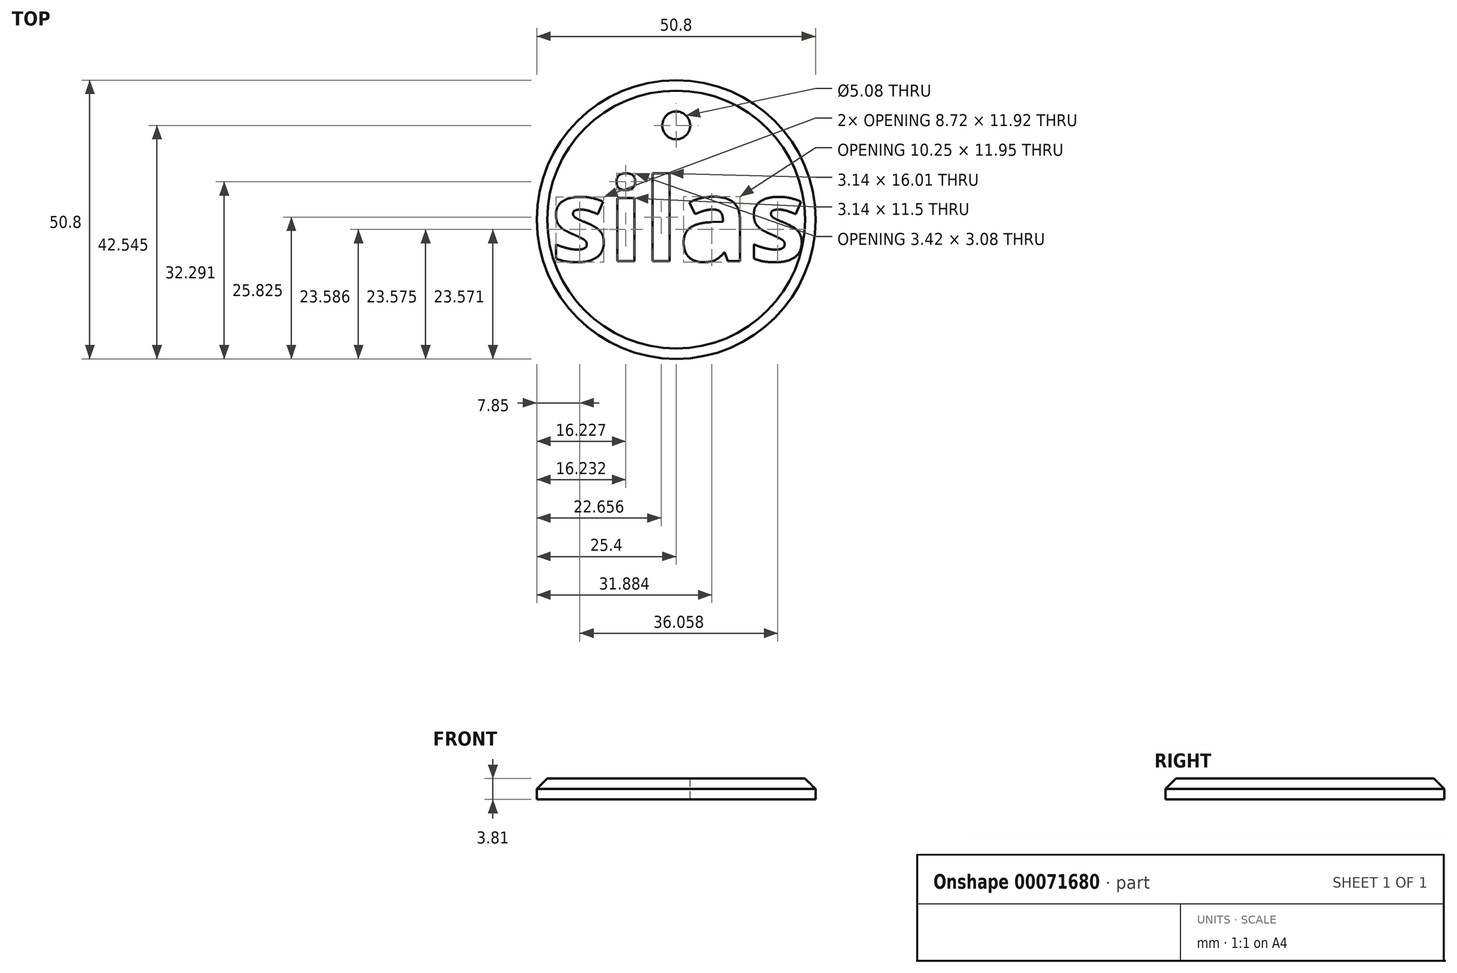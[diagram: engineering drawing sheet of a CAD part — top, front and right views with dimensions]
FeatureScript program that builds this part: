
annotation { "Feature Type Name" : "Feature", "Feature Type Description" : "" }
export const myFeature = defineFeature(function(context is Context, id is Id, definition is map)
    precondition{}
    {
        {
            var Q0;
            Q0=qCreatedBy(makeId("Top.planeOp"),FACE);
            var sketch = newSketch(context, id + "F0", { "sketchPlane" : qUnion([Q0])});
            skCircle(sketch, "E0", {"center": v(0, 0) * mm, "radius": 25.4 * mm});
            skText(sketch, "E1", { "text": "silas", "fontName": "OpenSans-Bold.ttf"});
            const initialGuessF0  = {"E1": [-0.02286, -0.00758, 1, 0, 0.01517]};
            skSetInitialGuess(sketch, initialGuessF0);
            skSolve(sketch);
        }
        {
            var Q0;
            Q0=makeQuery(id+"F0.imprint","IMPRINT",FACE,{"disambiguationData":[TD([[makeQuery(id+"F0.imprint","IMPRINT",EDGE,{"derivedFrom":sQuery(id+"F0.wireOp",EDGE,"E0")}),1.0]])]});
            extrude(context, id + "F1", {"entities" : qUnion([Q0]), "depth" : 3.8 * mm});
        }
        {
            var Q0;
            Q0=makeQuery(id+"F1.opExtrude","CAP_EDGE",EDGE,{"disambiguationData":[OSD([sQuery(id+"F0.wireOp",EDGE,"E0")])],"isStart":false});
            chamfer(context, id + "F2", {"entities" : qUnion([Q0]), "width" : 1.9 * mm, "tangentPropagation" : true});
        }
        {
            var Q0;
            Q0=makeQuery(id+"F1.opExtrude","CAP_FACE",FACE,{"disambiguationData":[OSD([sQuery(id+"F0.wireOp",EDGE,"E0"),sQuery(id+"F0.wireOp",EDGE,"E1.sketch_text.stroke-0"),sQuery(id+"F0.wireOp",EDGE,"E1.sketch_text.stroke-1"),sQuery(id+"F0.wireOp",EDGE,"E1.sketch_text.stroke-2"),sQuery(id+"F0.wireOp",EDGE,"E1.sketch_text.stroke-3"),sQuery(id+"F0.wireOp",EDGE,"E1.sketch_text.stroke-4"),sQuery(id+"F0.wireOp",EDGE,"E1.sketch_text.stroke-5"),sQuery(id+"F0.wireOp",EDGE,"E1.sketch_text.stroke-6"),sQuery(id+"F0.wireOp",EDGE,"E1.sketch_text.stroke-7"),sQuery(id+"F0.wireOp",EDGE,"E1.sketch_text.stroke-8"),sQuery(id+"F0.wireOp",EDGE,"E1.sketch_text.stroke-9"),sQuery(id+"F0.wireOp",EDGE,"E1.sketch_text.stroke-10"),sQuery(id+"F0.wireOp",EDGE,"E1.sketch_text.stroke-11"),sQuery(id+"F0.wireOp",EDGE,"E1.sketch_text.stroke-12"),sQuery(id+"F0.wireOp",EDGE,"E1.sketch_text.stroke-13"),sQuery(id+"F0.wireOp",EDGE,"E1.sketch_text.stroke-14"),sQuery(id+"F0.wireOp",EDGE,"E1.sketch_text.stroke-15"),sQuery(id+"F0.wireOp",EDGE,"E1.sketch_text.stroke-16"),sQuery(id+"F0.wireOp",EDGE,"E1.sketch_text.stroke-17"),sQuery(id+"F0.wireOp",EDGE,"E1.sketch_text.stroke-18"),sQuery(id+"F0.wireOp",EDGE,"E1.sketch_text.stroke-19"),sQuery(id+"F0.wireOp",EDGE,"E1.sketch_text.stroke-20"),sQuery(id+"F0.wireOp",EDGE,"E1.sketch_text.stroke-21"),sQuery(id+"F0.wireOp",EDGE,"E1.sketch_text.stroke-22"),sQuery(id+"F0.wireOp",EDGE,"E1.sketch_text.stroke-23"),sQuery(id+"F0.wireOp",EDGE,"E1.sketch_text.stroke-24"),sQuery(id+"F0.wireOp",EDGE,"E1.sketch_text.stroke-25"),sQuery(id+"F0.wireOp",EDGE,"E1.sketch_text.stroke-26"),sQuery(id+"F0.wireOp",EDGE,"E1.sketch_text.stroke-27"),sQuery(id+"F0.wireOp",EDGE,"E1.sketch_text.stroke-28"),sQuery(id+"F0.wireOp",EDGE,"E1.sketch_text.stroke-29"),sQuery(id+"F0.wireOp",EDGE,"E1.sketch_text.stroke-30"),sQuery(id+"F0.wireOp",EDGE,"E1.sketch_text.stroke-31"),sQuery(id+"F0.wireOp",EDGE,"E1.sketch_text.stroke-32"),sQuery(id+"F0.wireOp",EDGE,"E1.sketch_text.stroke-33"),sQuery(id+"F0.wireOp",EDGE,"E1.sketch_text.stroke-34"),sQuery(id+"F0.wireOp",EDGE,"E1.sketch_text.stroke-35"),sQuery(id+"F0.wireOp",EDGE,"E1.sketch_text.stroke-36"),sQuery(id+"F0.wireOp",EDGE,"E1.sketch_text.stroke-37"),sQuery(id+"F0.wireOp",EDGE,"E1.sketch_text.stroke-38"),sQuery(id+"F0.wireOp",EDGE,"E1.sketch_text.stroke-39"),sQuery(id+"F0.wireOp",EDGE,"E1.sketch_text.stroke-40"),sQuery(id+"F0.wireOp",EDGE,"E1.sketch_text.stroke-41"),sQuery(id+"F0.wireOp",EDGE,"E1.sketch_text.stroke-42"),sQuery(id+"F0.wireOp",EDGE,"E1.sketch_text.stroke-43"),sQuery(id+"F0.wireOp",EDGE,"E1.sketch_text.stroke-44"),sQuery(id+"F0.wireOp",EDGE,"E1.sketch_text.stroke-45"),sQuery(id+"F0.wireOp",EDGE,"E1.sketch_text.stroke-46"),sQuery(id+"F0.wireOp",EDGE,"E1.sketch_text.stroke-47"),sQuery(id+"F0.wireOp",EDGE,"E1.sketch_text.stroke-48"),sQuery(id+"F0.wireOp",EDGE,"E1.sketch_text.stroke-49"),sQuery(id+"F0.wireOp",EDGE,"E1.sketch_text.stroke-50"),sQuery(id+"F0.wireOp",EDGE,"E1.sketch_text.stroke-51"),sQuery(id+"F0.wireOp",EDGE,"E1.sketch_text.stroke-52"),sQuery(id+"F0.wireOp",EDGE,"E1.sketch_text.stroke-53"),sQuery(id+"F0.wireOp",EDGE,"E1.sketch_text.stroke-54"),sQuery(id+"F0.wireOp",EDGE,"E1.sketch_text.stroke-55"),sQuery(id+"F0.wireOp",EDGE,"E1.sketch_text.stroke-56"),sQuery(id+"F0.wireOp",EDGE,"E1.sketch_text.stroke-64"),sQuery(id+"F0.wireOp",EDGE,"E1.sketch_text.stroke-65"),sQuery(id+"F0.wireOp",EDGE,"E1.sketch_text.stroke-66"),sQuery(id+"F0.wireOp",EDGE,"E1.sketch_text.stroke-67"),sQuery(id+"F0.wireOp",EDGE,"E1.sketch_text.stroke-68"),sQuery(id+"F0.wireOp",EDGE,"E1.sketch_text.stroke-69"),sQuery(id+"F0.wireOp",EDGE,"E1.sketch_text.stroke-70"),sQuery(id+"F0.wireOp",EDGE,"E1.sketch_text.stroke-71"),sQuery(id+"F0.wireOp",EDGE,"E1.sketch_text.stroke-72"),sQuery(id+"F0.wireOp",EDGE,"E1.sketch_text.stroke-73"),sQuery(id+"F0.wireOp",EDGE,"E1.sketch_text.stroke-74"),sQuery(id+"F0.wireOp",EDGE,"E1.sketch_text.stroke-75"),sQuery(id+"F0.wireOp",EDGE,"E1.sketch_text.stroke-76"),sQuery(id+"F0.wireOp",EDGE,"E1.sketch_text.stroke-77"),sQuery(id+"F0.wireOp",EDGE,"E1.sketch_text.stroke-78"),sQuery(id+"F0.wireOp",EDGE,"E1.sketch_text.stroke-79"),sQuery(id+"F0.wireOp",EDGE,"E1.sketch_text.stroke-80"),sQuery(id+"F0.wireOp",EDGE,"E1.sketch_text.stroke-81"),sQuery(id+"F0.wireOp",EDGE,"E1.sketch_text.stroke-82"),sQuery(id+"F0.wireOp",EDGE,"E1.sketch_text.stroke-83"),sQuery(id+"F0.wireOp",EDGE,"E1.sketch_text.stroke-84"),sQuery(id+"F0.wireOp",EDGE,"E1.sketch_text.stroke-85"),sQuery(id+"F0.wireOp",EDGE,"E1.sketch_text.stroke-86"),sQuery(id+"F0.wireOp",EDGE,"E1.sketch_text.stroke-87"),sQuery(id+"F0.wireOp",EDGE,"E1.sketch_text.stroke-88"),sQuery(id+"F0.wireOp",EDGE,"E1.sketch_text.stroke-89")])],"isStart":false});
            var sketch = newSketch(context, id + "F3", { "sketchPlane" : qUnion([Q0])});
            skCircle(sketch, "E2", {"center": v(0, 17.14) * mm, "radius": 2.54 * mm});
            skSolve(sketch);
        }
        {
            var Q0;
            Q0=makeQuery(id+"F3.imprint","IMPRINT",FACE,{"disambiguationData":[TD([[makeQuery(id+"F3.imprint","IMPRINT",EDGE,{"derivedFrom":sQuery(id+"F3.wireOp",EDGE,"E2")}),1.0]])]});
            extrude(context, id + "F4", {"entities" : qUnion([Q0]), "operationType" : NewBodyOperationType.REMOVE, "oppositeDirection" : true, "depth" : 25.4 * mm});
        }
    });
